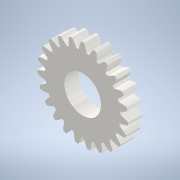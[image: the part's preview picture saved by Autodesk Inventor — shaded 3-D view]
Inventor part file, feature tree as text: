
AUTODESK INVENTOR PART (.ipt)
format: ipt  version: 2021 (Build 250183000, 183)  size: 244,224 bytes
history: native  units: mm (DEFAULTED — no unit token found)
features: plane x3, other x3, sketch x3, extrude x2
ambient origin geometry x8: Origin, YZ Plane, XZ Plane, XY Plane, X Axis, Y Axis, Z Axis, Center Point
bodies: Solid1 (feature_tree)
feature tree (11):
  extrude  "Extrusion1"  Depth=10.0mm TaperAngle=0.0deg
  plane  "Work Plane2"
  plane  "Work Plane8"
  plane  "Work Plane9"
  other  "Spur Gear"
  extrude  "Extrusion2"  Depth=10.0mm TaperAngle=0.0deg
  sketch  "Sketch1"  dims[d0=61.780644mm d1=10.0mm d2=0.0mm]
  sketch  "Sketch2"  dims[d3=57.5mm d4=10.0mm d5=0.0mm]
  other  "Srf1"
  sketch  "Sketch3"  dims[d16=60.0mm d17=0.0mm d34=1.36591mm d39=0.0mm d41=0.0mm d43=60.0mm d46=60.0mm d47=0.0mm d48=0.0mm d49=25.0mm d50=10.0mm d51=0.0mm]
  other  "Pitch Diameter"
